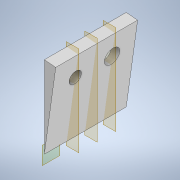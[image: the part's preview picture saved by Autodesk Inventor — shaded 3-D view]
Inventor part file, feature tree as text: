
AUTODESK INVENTOR PART (.ipt)
format: ipt  version: 2021 (Build 250183000, 183)  size: 238,592 bytes
history: native  units: in
note: dims shown in document units (in); Inventor stores cm internally (conversion verified against a paired STEP export)
features: extrude x4, sketch x4, plane x3, split x1
ambient origin geometry x8: Origin, YZ Plane, XZ Plane, XY Plane, X Axis, Y Axis, Z Axis, Center Point
bodies: Solid1 (feature_tree)
feature tree (12):
  extrude  "Extrusion1"  Depth=0.055in
  plane  "Work Plane2"
  extrude  "Extrusion5"  Depth=4.0in TaperAngle=0.0deg
  plane  "Work Plane3"
  plane  "Work Plane4"
  extrude  "TextforBack"  Depth=0.75in
  extrude  "Extrusion8"  Depth=0.9in
  split  "Split5"
  sketch  "Sketch1"  dims[d0=4.0in d1=0.055in]
  sketch  "Sketch6"  dims[d2=0.5622in d3=4.0in d4=0.0in]
  sketch  "Sketch9"  dims[d18=1.1in d19=0.75in]
  sketch  "Sketch10"  dims[d20=0.6in d21=0.9in d22=0.9in d23=1.8in d24=0.0in d25=0.0in d30=0.9in d31=-0.9in d35=1.5in d36=0.1in d37=0.0in d38=0.0344in d39=0.0in d40=0.0in]
